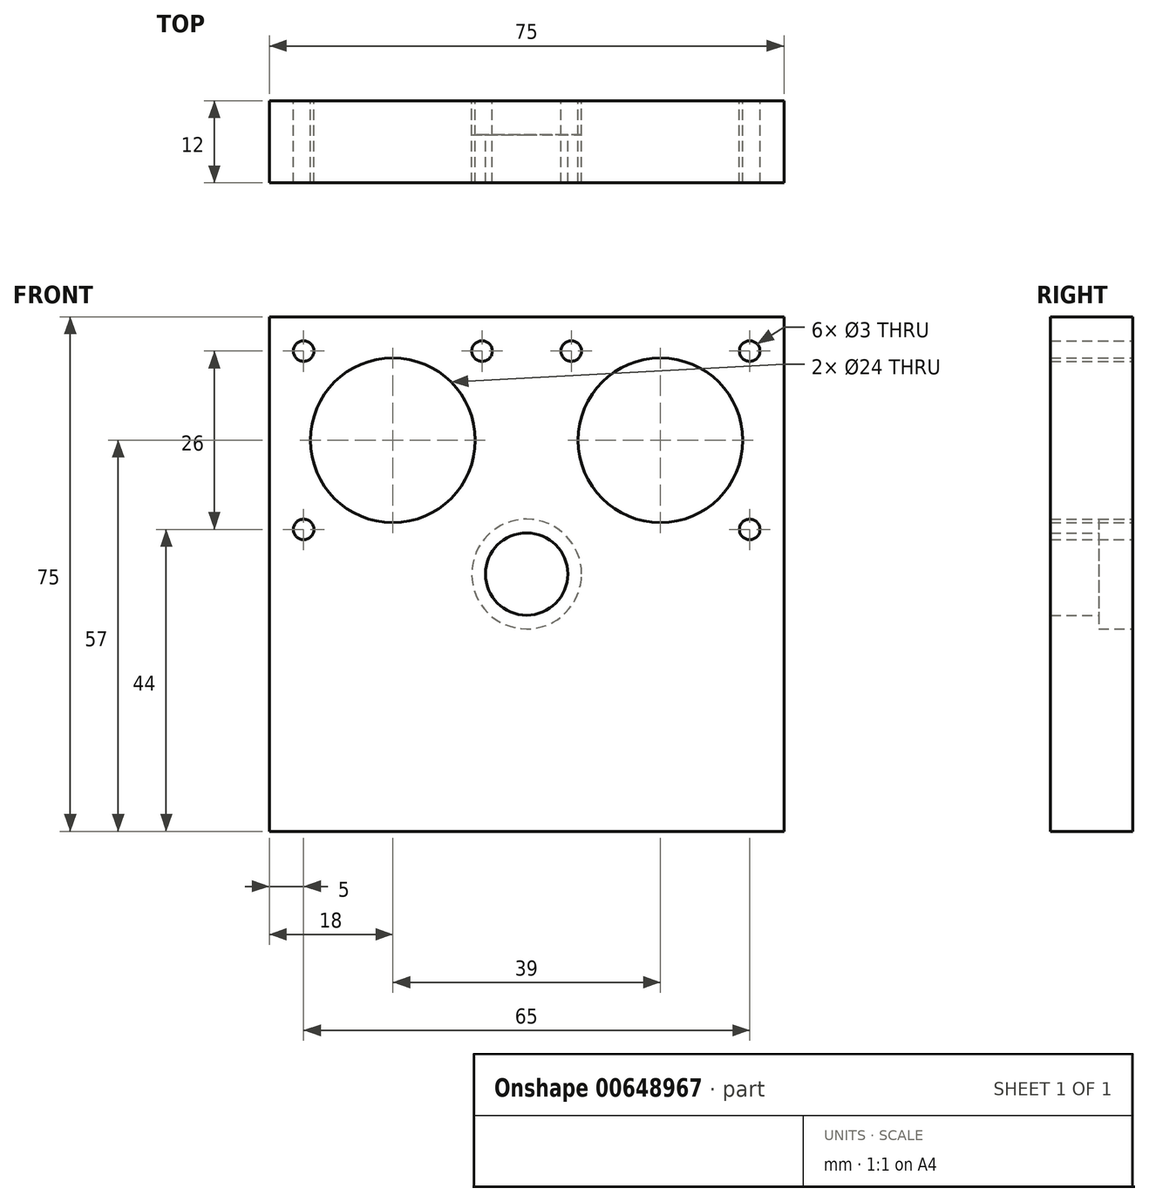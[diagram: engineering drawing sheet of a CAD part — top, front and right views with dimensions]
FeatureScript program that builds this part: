
annotation { "Feature Type Name" : "Feature", "Feature Type Description" : "" }
export const myFeature = defineFeature(function(context is Context, id is Id, definition is map)
    precondition{}
    {
        {
            var Q0;
            Q0=qCreatedBy(makeId("Front.planeOp"),FACE);
            var sketch = newSketch(context, id + "F0", { "sketchPlane" : qUnion([Q0])});
            skLineSegment(sketch, "E0.bottom", {"start": v(-37.5, 37.5) * mm, "end": v(37.5, 37.5) * mm});
            skLineSegment(sketch, "E0.top", {"start": v(-37.5, -37.5) * mm, "end": v(37.5, -37.5) * mm});
            skLineSegment(sketch, "E0.left", {"start": v(-37.5, 37.5) * mm, "end": v(-37.5, -37.5) * mm});
            skLineSegment(sketch, "E0.right", {"start": v(37.5, 37.5) * mm, "end": v(37.5, -37.5) * mm});
            skPoint(sketch, "E0.middle", {"position": v(0, 0) * mm});
            skSolve(sketch);
        }
        {
            var Q0;
            Q0 = qSketchRegion(id + "F0", true);
            extrude(context, id + "F1", {"entities" : qUnion([Q0]), "endBound" : BoundingType.SYMMETRIC, "depth" : 12 * mm, "offsetDistance" : 25 * mm});
        }
        {
            var Q0;
            Q0=makeQuery(id+"F1.opExtrude","CAP_FACE",FACE,{"disambiguationData":[OSD([sQuery(id+"F0.wireOp",EDGE,"E0.bottom"),sQuery(id+"F0.wireOp",EDGE,"E0.top"),sQuery(id+"F0.wireOp",EDGE,"E0.left"),sQuery(id+"F0.wireOp",EDGE,"E0.right")])],"isStart":true});
            var sketch = newSketch(context, id + "F2", { "sketchPlane" : qUnion([Q0])});
            skLineSegment(sketch, "E1", {"start": v(-19.5, 37.5) * mm, "end": v(-19.5, -37.5) * mm, "construction": true});
            skCircle(sketch, "E2", {"center": v(-19.5, 19.5) * mm, "radius": 12 * mm});
            skCircle(sketch, "E3", {"center": v(-32.5, 32.5) * mm, "radius": 1.5 * mm});
            skLineSegment(sketch, "E4", {"start": v(0, 37.5) * mm, "end": v(0, -37.5) * mm, "construction": true});
            skCircle(sketch, "E5.1.0", {"center": v(-32.5, 6.5) * mm, "radius": 1.5 * mm});
            skLineSegment(sketch, "E5.1.1", {"start": v(-37.5, 19.5) * mm, "end": v(37.5, 19.5) * mm, "construction": true});
            skCircle(sketch, "E5.2.0", {"center": v(-6.5, 6.5) * mm, "radius": 1.5 * mm, "construction": true});
            skLineSegment(sketch, "E5.2.1", {"start": v(-19.5, 1.5) * mm, "end": v(-19.5, 76.5) * mm, "construction": true});
            skCircle(sketch, "E5.3.0", {"center": v(-6.5, 32.5) * mm, "radius": 1.5 * mm});
            skLineSegment(sketch, "E5.3.1", {"start": v(-1.5, 19.5) * mm, "end": v(-76.5, 19.5) * mm, "construction": true});
            skCircle(sketch, "E6.MirrorC", {"center": v(6.5, 6.5) * mm, "radius": 1.5 * mm, "construction": true});
            skCircle(sketch, "E7.MirrorC", {"center": v(32.5, 6.5) * mm, "radius": 1.5 * mm});
            skCircle(sketch, "E8.MirrorC", {"center": v(32.5, 32.5) * mm, "radius": 1.5 * mm});
            skCircle(sketch, "E9.MirrorC", {"center": v(19.5, 19.5) * mm, "radius": 12 * mm});
            skCircle(sketch, "E10.MirrorC", {"center": v(6.5, 32.5) * mm, "radius": 1.5 * mm});
            skSolve(sketch);
        }
        {
            var Q0;
            Q0 = qSketchRegion(id + "F2", true);
            extrude(context, id + "F3", {"entities" : qUnion([Q0]), "operationType" : NewBodyOperationType.REMOVE, "endBound" : BoundingType.THROUGH_ALL, "oppositeDirection" : true, "depth" : 25 * mm, "offsetDistance" : 25 * mm});
        }
        {
            var Q0;
            Q0=makeQuery(id+"F1.opExtrude","CAP_FACE",FACE,{"disambiguationData":[OSD([sQuery(id+"F0.wireOp",EDGE,"E0.bottom"),sQuery(id+"F0.wireOp",EDGE,"E0.top"),sQuery(id+"F0.wireOp",EDGE,"E0.left"),sQuery(id+"F0.wireOp",EDGE,"E0.right")])],"isStart":true});
            var sketch = newSketch(context, id + "F4", { "sketchPlane" : qUnion([Q0])});
            skCircle(sketch, "E11", {"center": v(0, 0) * mm, "radius": 8 * mm});
            skSolve(sketch);
        }
        {
            var Q0;
            Q0 = qSketchRegion(id + "F4", true);
            extrude(context, id + "F5", {"entities" : qUnion([Q0]), "operationType" : NewBodyOperationType.REMOVE, "oppositeDirection" : true, "depth" : 5 * mm, "offsetDistance" : 25 * mm});
        }
        {
            var Q0;
            Q0=makeQuery(id+"F5.boolean.opBoolean","COPY",FACE,{"derivedFrom":makeQuery(id+"F5.opExtrude","CAP_FACE",FACE,{"disambiguationData":[OSD([sQuery(id+"F4.wireOp",EDGE,"E11")])],"isStart":false})});
            var sketch = newSketch(context, id + "F6", { "sketchPlane" : qUnion([Q0])});
            skCircle(sketch, "E12", {"center": v(0, 0) * mm, "radius": 6 * mm});
            skSolve(sketch);
        }
        {
            var Q0;
            Q0 = qSketchRegion(id + "F6", true);
            extrude(context, id + "F7", {"entities" : qUnion([Q0]), "operationType" : NewBodyOperationType.REMOVE, "endBound" : BoundingType.THROUGH_ALL, "oppositeDirection" : true, "depth" : 25 * mm, "offsetDistance" : 25 * mm});
        }
    });
